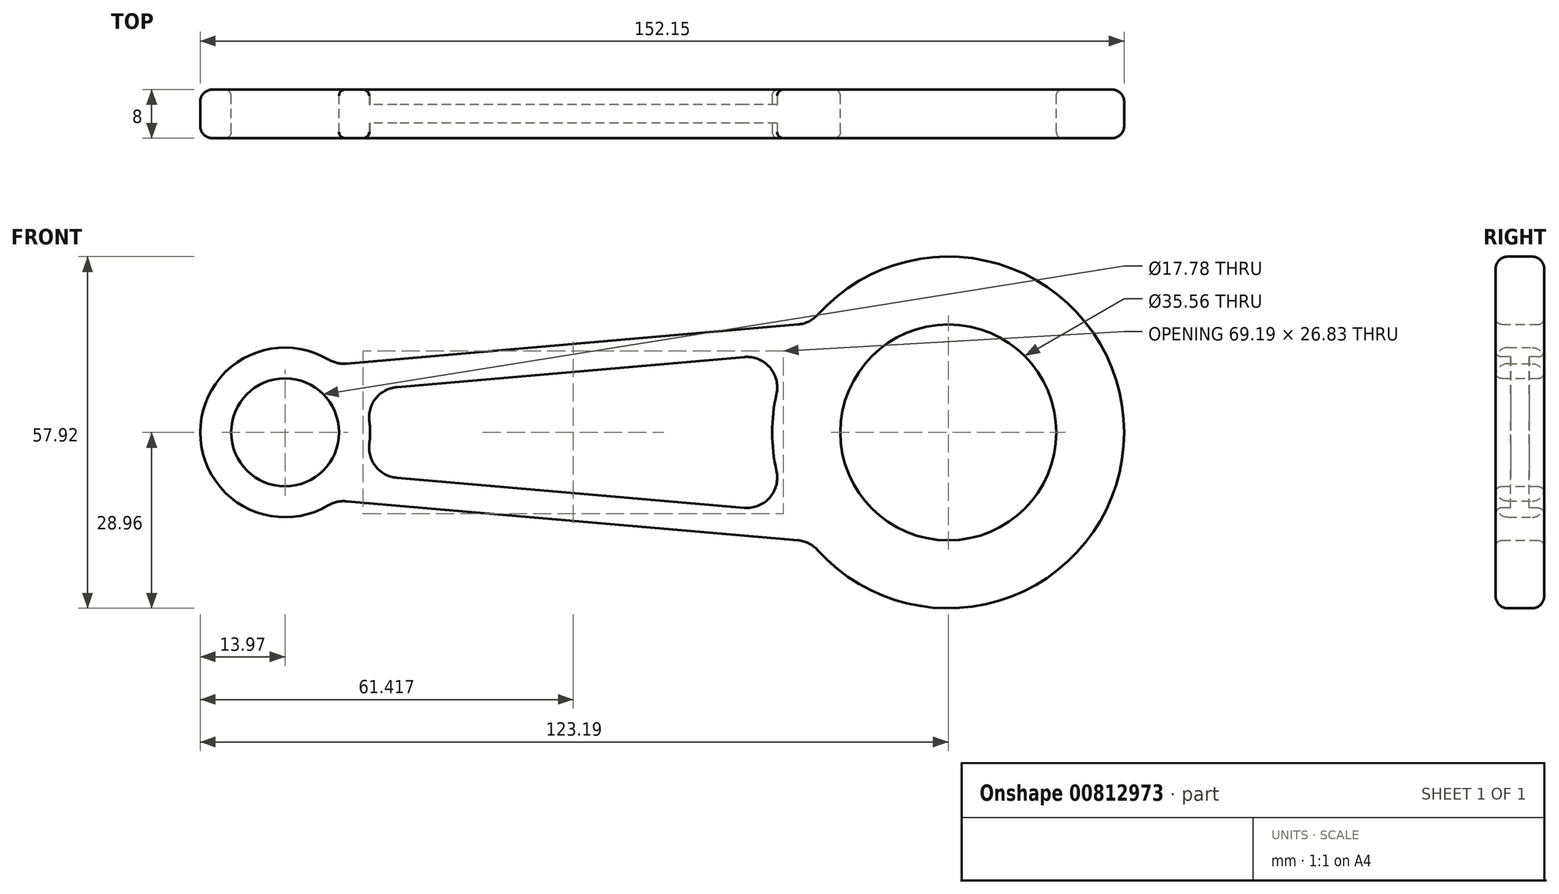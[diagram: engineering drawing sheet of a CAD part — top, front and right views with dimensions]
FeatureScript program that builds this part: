
annotation { "Feature Type Name" : "Feature", "Feature Type Description" : "" }
export const myFeature = defineFeature(function(context is Context, id is Id, definition is map)
    precondition{}
    {
        {
            var Q0;
            Q0=qCreatedBy(makeId("Front.planeOp"),FACE);
            var sketch = newSketch(context, id + "F0", { "sketchPlane" : qUnion([Q0])});
            skCircle(sketch, "E0", {"center": v(0, 0) * mm, "radius": 8.9 * mm});
            skLineSegment(sketch, "E1", {"start": v(0, 0) * mm, "end": v(109.22, 0) * mm});
            skCircle(sketch, "E2", {"center": v(109.22, 0) * mm, "radius": 17.78 * mm});
            skCircle(sketch, "E3", {"center": v(0, 0) * mm, "radius": 13.97 * mm});
            skCircle(sketch, "E4", {"center": v(109.22, 0) * mm, "radius": 28.96 * mm});
            skLineSegment(sketch, "E5", {"start": v(8.37, 11.19) * mm, "end": v(86.5, 17.94) * mm});
            skLineSegment(sketch, "E6.MirrorCS", {"start": v(8.37, -11.19) * mm, "end": v(86.5, -17.94) * mm});
            skSolve(sketch);
        }
        {
            var Q0;
            Q0=makeQuery(id+"F0.imprint","IMPRINT",FACE,{"disambiguationData":[TD([[makeQuery(id+"F0.imprint","IMPRINT",EDGE,{"derivedFrom":sQuery(id+"F0.wireOp",EDGE,"E0")}),-1.0]])]});
            var Q1;
            Q1=makeQuery(id+"F0.imprint","IMPRINT",FACE,{"disambiguationData":[TD([[makeQuery(id+"F0.imprint","IMPRINT",EDGE,{"derivedFrom":sQuery(id+"F0.wireOp",EDGE,"E2")}),-1.0]])]});
            var Q2;
            {var subQ5=sQuery(id+"F0.wireOp",EDGE,"E5");Q2=makeQuery(id+"F0.imprint","IMPRINT",FACE,{"disambiguationData":[TD([[makeQuery(id+"F0.imprint","IMPRINT",EDGE,{"derivedFrom":subQ5}),-1.0]])]});}
            var Q3;
            {var subQ5=sQuery(id+"F0.wireOp",EDGE,"E6.MirrorCS");Q3=makeQuery(id+"F0.imprint","IMPRINT",FACE,{"disambiguationData":[TD([[makeQuery(id+"F0.imprint","IMPRINT",EDGE,{"derivedFrom":subQ5}),1.0]])]});}
            extrude(context, id + "F1", {"entities" : qUnion([Q0, Q1, Q2, Q3]), "endBound" : BoundingType.SYMMETRIC, "depth" : 8 * mm, "offsetDistance" : 25 * mm});
        }
        {
            var Q0;
            Q0=makeQuery(id+"F1.opExtrude","CAP_FACE",FACE,{"disambiguationData":[OSD([sQuery(id+"F0.wireOp",EDGE,"E0"),sQuery(id+"F0.wireOp",EDGE,"E2"),sQuery(id+"F0.wireOp",EDGE,"E3"),sQuery(id+"F0.wireOp",EDGE,"E4"),sQuery(id+"F0.wireOp",EDGE,"E5"),sQuery(id+"F0.wireOp",EDGE,"E6.MirrorCS")])],"isStart":false});
            var sketch = newSketch(context, id + "F2", { "sketchPlane" : qUnion([Q0])});
            skCircle(sketch, "E7", {"center": v(0, 0) * mm, "radius": 14 * mm});
            skCircle(sketch, "E8", {"center": v(109.22, 0) * mm, "radius": 29 * mm});
            skLineSegment(sketch, "E9", {"start": v(16.73, -7.32) * mm, "end": v(77.9, -12.61) * mm});
            skLineSegment(sketch, "E10.MirrorCS", {"start": v(16.73, 7.32) * mm, "end": v(77.9, 12.61) * mm});
            skLineSegment(sketch, "E11", {"start": v(12.16, -2.34) * mm, "end": v(12.16, 2.34) * mm});
            skLineSegment(sketch, "E12", {"start": v(83.34, -7.63) * mm, "end": v(83.34, 7.63) * mm});
            skPoint(sketch, "E13.visualSharp", {"position": v(12.16, -6.93) * mm});
            skArc(sketch, "E13.filletArc", {"start": v(12.16, -2.34) * mm, "mid": v(13.48, -5.72) * mm, "end": v(16.73, -7.32) * mm});
            skPoint(sketch, "E14.visualSharp", {"position": v(12.16, 6.93) * mm});
            skArc(sketch, "E14.filletArc", {"start": v(16.73, 7.32) * mm, "mid": v(13.48, 5.72) * mm, "end": v(12.16, 2.34) * mm});
            skPoint(sketch, "E15.visualSharp", {"position": v(83.34, -13.08) * mm});
            skArc(sketch, "E15.filletArc", {"start": v(77.9, -12.61) * mm, "mid": v(81.72, -11.32) * mm, "end": v(83.34, -7.63) * mm});
            skPoint(sketch, "E16.visualSharp", {"position": v(83.34, 13.08) * mm});
            skArc(sketch, "E16.filletArc", {"start": v(83.34, 7.63) * mm, "mid": v(81.72, 11.32) * mm, "end": v(77.9, 12.61) * mm});
            skSolve(sketch);
        }
        {
            var Q0;
            {var subQ6=sQuery(id+"F2.wireOp",EDGE,"E9");Q0=makeQuery(id+"F2.imprint","IMPRINT",FACE,{"disambiguationData":[TD([[makeQuery(id+"F2.imprint","IMPRINT",EDGE,{"derivedFrom":subQ6}),1.0]])]});}
            extrude(context, id + "F3", {"entities" : qUnion([Q0]), "operationType" : NewBodyOperationType.REMOVE, "oppositeDirection" : true, "depth" : 27.8 * mm, "offsetDistance" : 25 * mm});
        }
        {
            var Q0;
            Q0=makeQuery(id+"F3.boolean.opBoolean","COPY",EDGE,{"derivedFrom":makeQuery(id+"F3.opExtrude","SWEPT_EDGE",EDGE,{"disambiguationData":[OSD([sQuery(id+"F2.wireOp",EDGE,"E7"),sQuery(id+"F2.wireOp",EDGE,"E13.filletArc")])]})});
            var Q1;
            Q1=makeQuery(id+"F3.boolean.opBoolean","COPY",EDGE,{"derivedFrom":makeQuery(id+"F3.opExtrude","SWEPT_EDGE",EDGE,{"disambiguationData":[OSD([sQuery(id+"F2.wireOp",EDGE,"E7"),sQuery(id+"F2.wireOp",EDGE,"E14.filletArc")])]})});
            fillet(context, id + "F4", {"entities" : qUnion([Q0, Q1]), "radius" : 5 * mm, "tangentPropagation" : true, "allowEdgeOverflow" : false});
        }
        {
            var Q0;
            Q0=makeQuery(id+"F3.boolean.opBoolean","COPY",EDGE,{"derivedFrom":makeQuery(id+"F3.opExtrude","SWEPT_EDGE",EDGE,{"disambiguationData":[OSD([sQuery(id+"F2.wireOp",EDGE,"E8"),sQuery(id+"F2.wireOp",EDGE,"E15.filletArc")])]})});
            var Q1;
            Q1=makeQuery(id+"F3.boolean.opBoolean","COPY",EDGE,{"derivedFrom":makeQuery(id+"F3.opExtrude","SWEPT_EDGE",EDGE,{"disambiguationData":[OSD([sQuery(id+"F2.wireOp",EDGE,"E8"),sQuery(id+"F2.wireOp",EDGE,"E16.filletArc")])]})});
            fillet(context, id + "F5", {"entities" : qUnion([Q0, Q1]), "radius" : 5 * mm, "tangentPropagation" : true, "allowEdgeOverflow" : false});
        }
        {
            var Q0;
            Q0=makeQuery(id+"F1.opExtrude","SWEPT_EDGE",EDGE,{"disambiguationData":[OSD([sQuery(id+"F0.wireOp",EDGE,"E3"),sQuery(id+"F0.wireOp",EDGE,"E5")])]});
            var Q1;
            Q1=makeQuery(id+"F1.opExtrude","SWEPT_EDGE",EDGE,{"disambiguationData":[OSD([sQuery(id+"F0.wireOp",EDGE,"E3"),sQuery(id+"F0.wireOp",EDGE,"E6.MirrorCS")])]});
            var Q2;
            Q2=makeQuery(id+"F1.opExtrude","SWEPT_EDGE",EDGE,{"disambiguationData":[OSD([sQuery(id+"F0.wireOp",EDGE,"E4"),sQuery(id+"F0.wireOp",EDGE,"E6.MirrorCS")])]});
            var Q3;
            Q3=makeQuery(id+"F1.opExtrude","SWEPT_EDGE",EDGE,{"disambiguationData":[OSD([sQuery(id+"F0.wireOp",EDGE,"E4"),sQuery(id+"F0.wireOp",EDGE,"E5")])]});
            fillet(context, id + "F6", {"entities" : qUnion([Q0, Q1, Q2, Q3]), "radius" : 5 * mm, "tangentPropagation" : true, "allowEdgeOverflow" : false});
        }
        {
            var Q0;
            Q0=makeQuery(id+"F1.opExtrude","CAP_EDGE",EDGE,{"disambiguationData":[OSD([sQuery(id+"F0.wireOp",EDGE,"E3")])],"isStart":false});
            var Q1;
            Q1=makeQuery(id+"F1.opExtrude","CAP_EDGE",EDGE,{"disambiguationData":[OSD([sQuery(id+"F0.wireOp",EDGE,"E3")])],"isStart":true});
            fillet(context, id + "F7", {"entities" : qUnion([Q0, Q1]), "radius" : 2 * mm, "tangentPropagation" : true, "allowEdgeOverflow" : false});
        }
        {
            var Q0;
            Q0=qCreatedBy(makeId("Front.planeOp"),FACE);
            var sketch = newSketch(context, id + "F8", { "sketchPlane" : qUnion([Q0])});
            skLineSegment(sketch, "E17", {"start": v(10.46, 8.71) * mm, "end": v(10.46, -8.71) * mm});
            skLineSegment(sketch, "E18", {"start": v(10.46, -8.71) * mm, "end": v(83.9, -14.7) * mm});
            skLineSegment(sketch, "E19", {"start": v(83.9, -14.7) * mm, "end": v(83.9, 15.05) * mm});
            skLineSegment(sketch, "E20", {"start": v(83.9, 15.05) * mm, "end": v(10.46, 8.71) * mm});
            skSolve(sketch);
        }
        {
            var Q0;
            Q0 = qSketchRegion(id + "F8", true);
            extrude(context, id + "F9", {"entities" : qUnion([Q0]), "operationType" : NewBodyOperationType.ADD, "endBound" : BoundingType.SYMMETRIC, "depth" : 3 * mm, "offsetDistance" : 25 * mm});
        }
        {
            var Q0;
            Q0=makeQuery(id+"F3.boolean.opBoolean","COPY",EDGE,{"derivedFrom":makeQuery(id+"F3.opExtrude","CAP_EDGE",EDGE,{"disambiguationData":[OSD([sQuery(id+"F2.wireOp",EDGE,"E7")])],"isStart":true})});
            var Q1;
            Q1=makeQuery(id+"F4.opFillet","BLEND_EDGE",EDGE,{"blendedFrom":[makeQuery(id+"F3.boolean.opBoolean","COPY",EDGE,{"derivedFrom":makeQuery(id+"F3.opExtrude","SWEPT_EDGE",EDGE,{"disambiguationData":[OSD([sQuery(id+"F2.wireOp",EDGE,"E7"),sQuery(id+"F2.wireOp",EDGE,"E14.filletArc")])]})}),makeQuery(id+"F1.opExtrude","CAP_FACE",FACE,{"disambiguationData":[OSD([sQuery(id+"F0.wireOp",EDGE,"E0"),sQuery(id+"F0.wireOp",EDGE,"E2"),sQuery(id+"F0.wireOp",EDGE,"E3"),sQuery(id+"F0.wireOp",EDGE,"E4"),sQuery(id+"F0.wireOp",EDGE,"E5"),sQuery(id+"F0.wireOp",EDGE,"E6.MirrorCS")])],"isStart":false})],"blendedInto":[makeQuery(id+"F1.opExtrude","CAP_FACE",FACE,{"disambiguationData":[OSD([sQuery(id+"F0.wireOp",EDGE,"E0"),sQuery(id+"F0.wireOp",EDGE,"E2"),sQuery(id+"F0.wireOp",EDGE,"E3"),sQuery(id+"F0.wireOp",EDGE,"E4"),sQuery(id+"F0.wireOp",EDGE,"E5"),sQuery(id+"F0.wireOp",EDGE,"E6.MirrorCS")])],"isStart":false})]});
            var Q2;
            Q2=makeQuery(id+"F3.boolean.opBoolean","COPY",EDGE,{"derivedFrom":makeQuery(id+"F3.opExtrude","CAP_EDGE",EDGE,{"disambiguationData":[OSD([sQuery(id+"F2.wireOp",EDGE,"E10.MirrorCS")])],"isStart":true})});
            var Q3;
            Q3=makeQuery(id+"F3.boolean.opBoolean","INTERSECT",EDGE,{"derivedFrom":[makeQuery(id+"F1.opExtrude","CAP_FACE",FACE,{"disambiguationData":[OSD([sQuery(id+"F0.wireOp",EDGE,"E0"),sQuery(id+"F0.wireOp",EDGE,"E2"),sQuery(id+"F0.wireOp",EDGE,"E3"),sQuery(id+"F0.wireOp",EDGE,"E4"),sQuery(id+"F0.wireOp",EDGE,"E5"),sQuery(id+"F0.wireOp",EDGE,"E6.MirrorCS")])],"isStart":true}),makeQuery(id+"F3.opExtrude","SWEPT_FACE",FACE,{"disambiguationData":[OSD([sQuery(id+"F2.wireOp",EDGE,"E7")])]})]});
            fillet(context, id + "F10", {"entities" : qUnion([Q0, Q1, Q2, Q3]), "radius" : 1 * mm, "tangentPropagation" : true, "allowEdgeOverflow" : false});
        }
        {
            var Q0;
            Q0=makeQuery(id+"F1.opExtrude","CAP_EDGE",EDGE,{"disambiguationData":[OSD([sQuery(id+"F0.wireOp",EDGE,"E0")])],"isStart":false});
            var Q1;
            Q1=makeQuery(id+"F1.opExtrude","CAP_EDGE",EDGE,{"disambiguationData":[OSD([sQuery(id+"F0.wireOp",EDGE,"E0")])],"isStart":true});
            var Q2;
            Q2=makeQuery(id+"F1.opExtrude","CAP_EDGE",EDGE,{"disambiguationData":[OSD([sQuery(id+"F0.wireOp",EDGE,"E2")])],"isStart":false});
            var Q3;
            Q3=makeQuery(id+"F1.opExtrude","CAP_EDGE",EDGE,{"disambiguationData":[OSD([sQuery(id+"F0.wireOp",EDGE,"E2")])],"isStart":true});
            fillet(context, id + "F11", {"entities" : qUnion([Q0, Q1, Q2, Q3]), "radius" : 1 * mm, "tangentPropagation" : true, "allowEdgeOverflow" : false});
        }
    });
